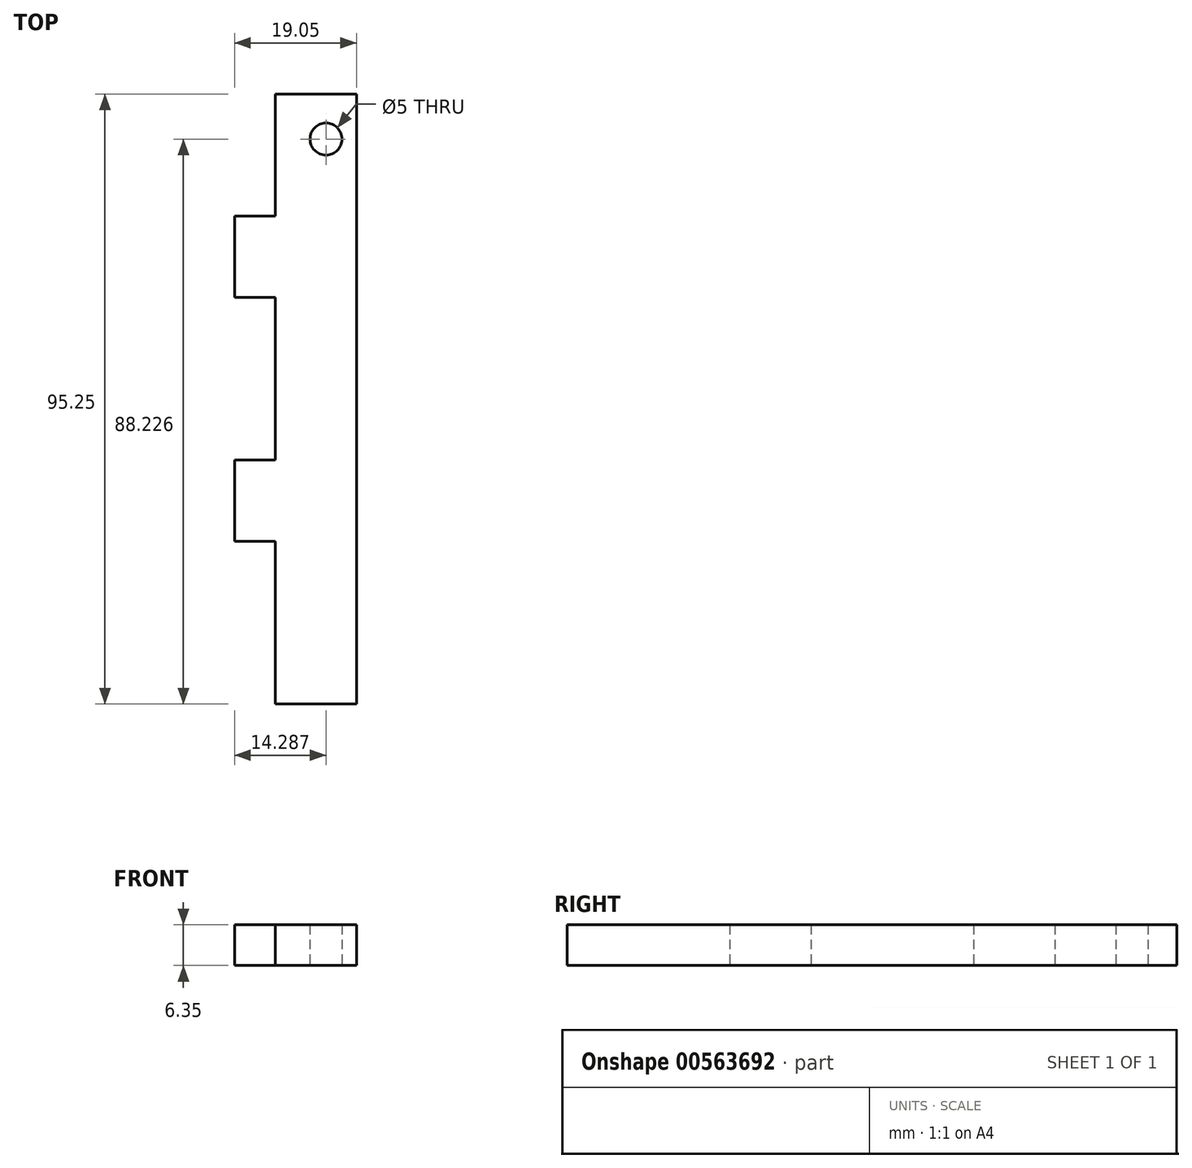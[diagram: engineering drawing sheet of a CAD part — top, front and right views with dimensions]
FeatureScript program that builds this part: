
annotation { "Feature Type Name" : "Feature", "Feature Type Description" : "" }
export const myFeature = defineFeature(function(context is Context, id is Id, definition is map)
    precondition{}
    {
        {
            var Q0;
            Q0=qCreatedBy(makeId("Top.planeOp"),FACE);
            var sketch = newSketch(context, id + "F0", { "sketchPlane" : qUnion([Q0])});
            skLineSegment(sketch, "E0.bottom", {"start": v(0, 0) * mm, "end": v(12.7, 0) * mm});
            skLineSegment(sketch, "E0.top", {"start": v(0, 95.25) * mm, "end": v(12.7, 95.25) * mm});
            skLineSegment(sketch, "E0.left", {"start": v(0, 0) * mm, "end": v(0, 95.25) * mm});
            skLineSegment(sketch, "E0.right", {"start": v(12.7, 0) * mm, "end": v(12.7, 95.25) * mm});
            skLineSegment(sketch, "E1.bottom", {"start": v(0, 76.2) * mm, "end": v(-6.35, 76.2) * mm});
            skLineSegment(sketch, "E1.top", {"start": v(0, 63.5) * mm, "end": v(-6.35, 63.5) * mm});
            skLineSegment(sketch, "E1.left", {"start": v(0, 76.2) * mm, "end": v(0, 63.5) * mm});
            skLineSegment(sketch, "E1.right", {"start": v(-6.35, 76.2) * mm, "end": v(-6.35, 63.5) * mm});
            skLineSegment(sketch, "E2.bottom", {"start": v(0, 38.1) * mm, "end": v(-6.35, 38.1) * mm});
            skLineSegment(sketch, "E2.top", {"start": v(0, 25.4) * mm, "end": v(-6.35, 25.4) * mm});
            skLineSegment(sketch, "E2.left", {"start": v(0, 38.1) * mm, "end": v(0, 25.4) * mm});
            skLineSegment(sketch, "E2.right", {"start": v(-6.35, 38.1) * mm, "end": v(-6.35, 25.4) * mm});
            skCircle(sketch, "E3", {"center": v(7.94, 88.23) * mm, "radius": 2.5 * mm});
            skSolve(sketch);
        }
        {
            var Q0;
            Q0 = qSketchRegion(id + "F0", true);
            extrude(context, id + "F1", {"entities" : qUnion([Q0]), "depth" : 6.35 * mm, "offsetDistance" : 25.4 * mm});
        }
    });
